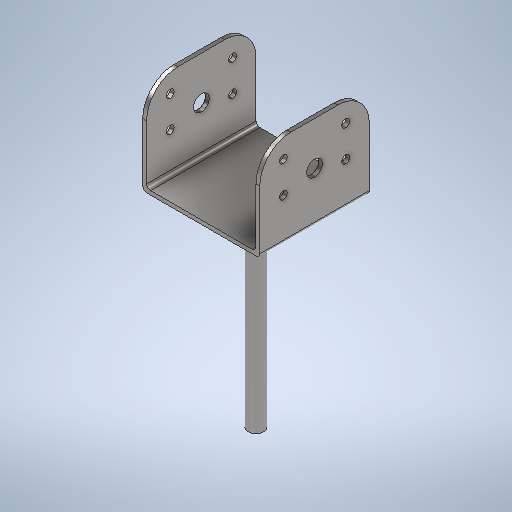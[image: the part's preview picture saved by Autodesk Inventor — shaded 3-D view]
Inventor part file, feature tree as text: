
AUTODESK INVENTOR PART (.ipt)
format: ipt  version: 2025.1 (Build 291241020, 241B)  size: 327,168 bytes
history: native  units: in
note: dims shown in document units (in); Inventor stores cm internally (conversion verified against a paired STEP export)
features: sketch x4, extrude x3, fillet x2, hole x2
ambient origin geometry x8: Origin, YZ Plane, XZ Plane, XY Plane, X Axis, Y Axis, Z Axis, Center Point
bodies: Solid1 (feature_tree)
feature tree (11):
  extrude  "Extrusion1"  Depth=3.5in
  extrude  "Extrusion2"  Depth=0.125in
  fillet  "Fillet1"  Radius=2.875in
  fillet  "Fillet2"  Radius=0.125in
  sketch  "Sketch3"  dims[d8=1.0in d10=0.25in]
  hole  "Hole1"  [1 undecoded]
  hole  "Hole2"  [1 undecoded]
  extrude  "Extrusion3"  Depth=1.0in
  sketch  "Sketch1"  dims[d0=3.75in d1=3.5in]
  sketch  "Sketch2"  dims[d2=0.125in d3=0.0in d4=0.125in d5=2.875in d6=0.0in d7=0.125in]
  sketch  "Sketch4"  dims[d11=0.75in d12=0.625in d13=1.0in d14=0.75in d15=0.5in d16=0.25in d17=0.25in d18=0.75in d19=0.375in d20=0.25in d21=0.5635in d22=1.0in d23=0.8108in d24=0.5in d25=0.75in d26=0.375in d27=0.25in d28=0.5635in d29=1.0in d30=0.8108in d31=0.5in d32=6.5in d33=0.0in d9=0.0in]
note: 2 required parameter values undecoded (feature->parameter linkage not recoverable at this tier; creation-order binding heuristic only, values carry confidence <= 0.55)
